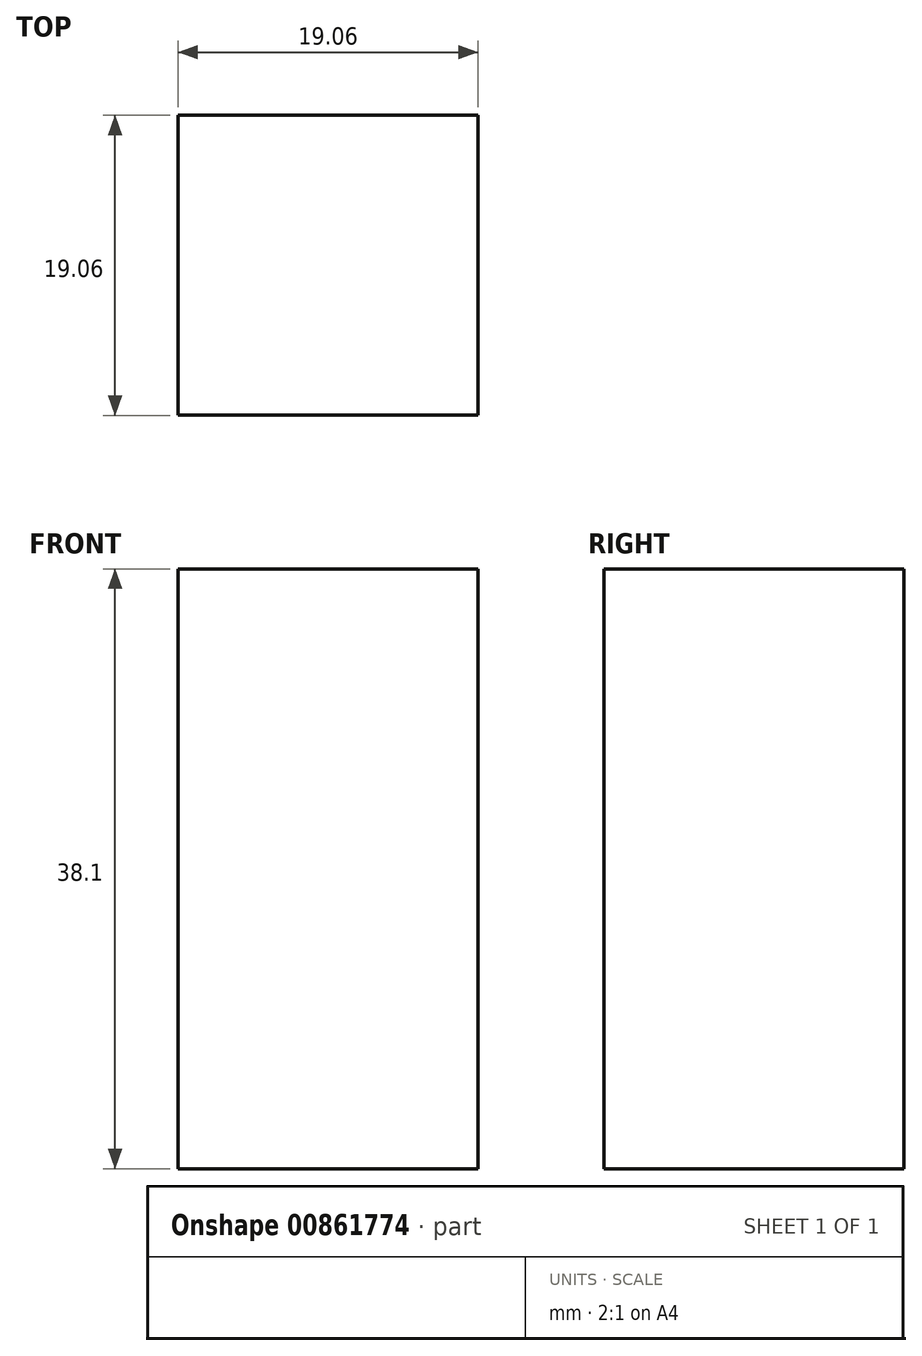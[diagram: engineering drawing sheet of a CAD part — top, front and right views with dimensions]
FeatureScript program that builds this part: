
annotation { "Feature Type Name" : "Feature", "Feature Type Description" : "" }
export const myFeature = defineFeature(function(context is Context, id is Id, definition is map)
    precondition{}
    {
        {
            var Q0;
            Q0=qCreatedBy(makeId("Top.planeOp"),FACE);
            var sketch = newSketch(context, id + "F0", { "sketchPlane" : qUnion([Q0])});
            skLineSegment(sketch, "E0.bottom", {"start": v(9.52, 9.53) * mm, "end": v(-9.53, 9.53) * mm});
            skLineSegment(sketch, "E0.top", {"start": v(9.52, -9.53) * mm, "end": v(-9.53, -9.53) * mm});
            skLineSegment(sketch, "E0.left", {"start": v(9.52, 9.53) * mm, "end": v(9.52, -9.52) * mm});
            skLineSegment(sketch, "E0.right", {"start": v(-9.53, 9.53) * mm, "end": v(-9.53, -9.53) * mm});
            skPoint(sketch, "E0.middle", {"position": v(0, 0) * mm});
            skSolve(sketch);
        }
        {
            var Q0;
            Q0=makeQuery(id+"F0.imprint","IMPRINT",FACE,{"disambiguationData":[TD([[makeQuery(id+"F0.imprint","IMPRINT",EDGE,{"derivedFrom":sQuery(id+"F0.wireOp",EDGE,"E0.bottom")}),1.0]])]});
            extrude(context, id + "F1", {"entities" : qUnion([Q0]), "depth" : 38.1 * mm, "offsetDistance" : 25 * mm});
        }
    });
